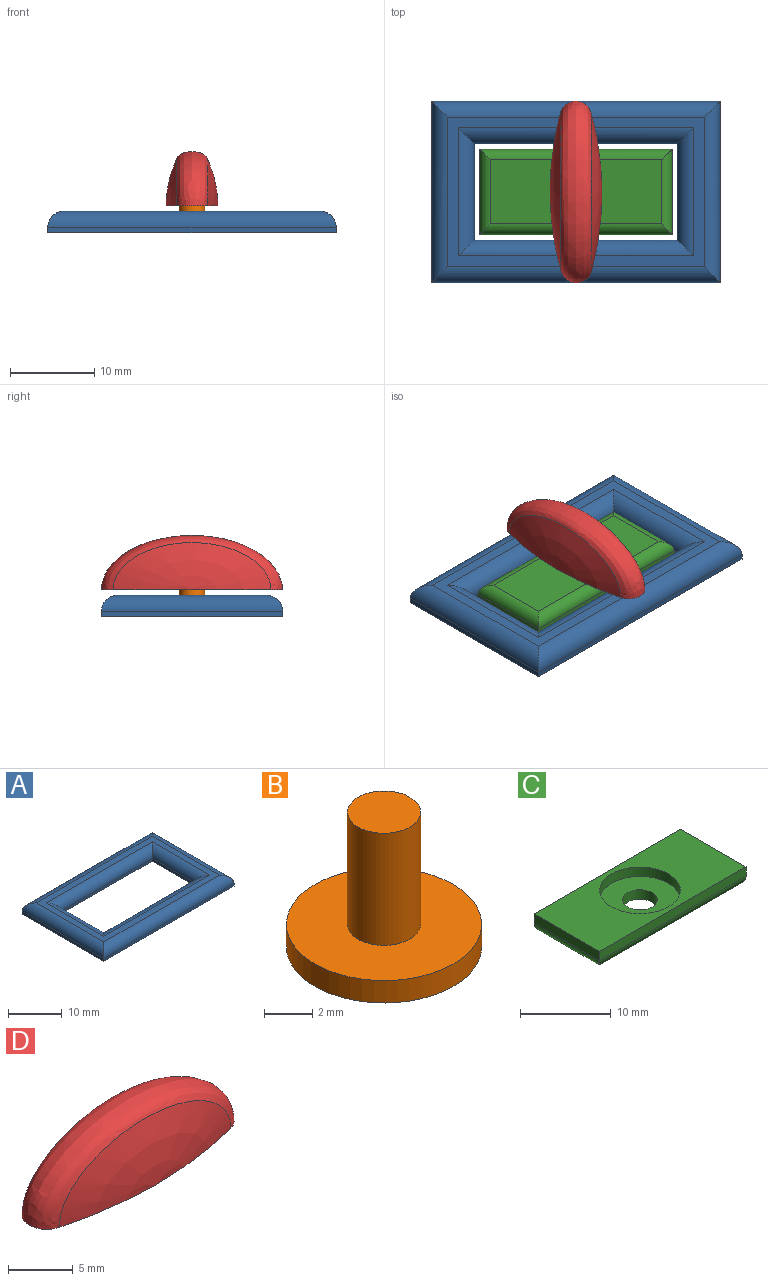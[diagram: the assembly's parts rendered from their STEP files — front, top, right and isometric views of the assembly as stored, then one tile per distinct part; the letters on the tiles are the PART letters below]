
ASSEMBLY  parts=4 mates=6
PART A: 18 faces, bbox 34.3x21.6x2.5 mm
  f0: plane 24.13x0.64mm, normal (0,1,0), area 15.3mm2, adj f1,f7,f9,f10
  f1: plane 11.43x0.64mm, normal (1,0,0), area 7.3mm2, adj f0,f2,f9,f11
  f2: plane 24.13x0.64mm, normal (0,-1,0), area 15.3mm2, adj f1,f7,f9,f13
  f3: plane 34.29x0.64mm, normal (0,-1,0), area 21.8mm2, adj f4,f6,f9,f15
  f4: plane 21.59x0.64mm, normal (1,0,0), area 13.7mm2, adj f3,f5,f9,f14
  f5: plane 34.29x0.64mm, normal (0,1,0), area 21.8mm2, adj f4,f6,f9,f16
  f6: plane 21.59x0.64mm, normal (-1,0,0), area 13.7mm2, adj f3,f5,f9,f17
  f7: plane 11.43x0.64mm, normal (-1,0,0), area 7.3mm2, adj f0,f2,f9,f12
  f8: plane 30.48x17.78mm, normal (0,0,1), area 116.1mm2, adj f10,f11,f12,f13,f14,f15,f16,f17
  f9: plane 34.29x21.59mm, normal (0,0,-1), area 464.5mm2, adj f0,f1,f2,f3,f4,f5,f6,f7
  f10: cylinder r=1.91mm len=27.94mm, axis (1,0,0), area 76.3mm2, adj f0,f8,f11,f12
  f11: cylinder r=1.91mm len=15.24mm, axis (0,-1,0), area 38.3mm2, adj f1,f8,f10,f13
  f12: cylinder r=1.91mm len=15.24mm, axis (0,1,0), area 38.3mm2, adj f7,f8,f10,f13
  f13: cylinder r=1.91mm len=27.94mm, axis (-1,0,0), area 76.3mm2, adj f2,f8,f11,f12
  f14: cylinder r=1.91mm len=21.59mm, axis (0,-1,0), area 60.5mm2, adj f4,f8,f15,f16
  f15: cylinder r=1.91mm len=34.29mm, axis (-1,0,0), area 98.5mm2, adj f3,f8,f14,f17
  f16: cylinder r=1.91mm len=34.29mm, axis (1,0,0), area 98.5mm2, adj f5,f8,f14,f17
  f17: cylinder r=1.91mm len=21.59mm, axis (0,1,0), area 60.5mm2, adj f6,f8,f15,f16
PART B: 5 faces, bbox 8.1x8.1x6.9 mm
  f0: cylinder r=4.06mm len=8.13mm, axis (0,0,-1), area 29.2mm2, adj f1,f2
  f1: plane 8.13x8.13mm, normal (0,0,1), area 44.6mm2, adj f0,f3
  f2: plane 8.13x8.13mm, normal (0,0,-1), area 51.9mm2, adj f0
  f3: cylinder r=1.52mm len=5.72mm, axis (0,0,-1), area 54.7mm2, adj f1,f4
  f4: plane 3.05x3.05mm, normal (0,0,1), area 7.3mm2, adj f3
PART C: 13 faces, bbox 22.9x10.2x2.5 mm
  f0: cylinder r=1.91mm len=3.81mm, axis (0,0,1), area 15.2mm2, adj f6,f12
  f1: plane 22.86x1.27mm, normal (0,-1,0), area 29mm2, adj f2,f4,f5,f7
  f2: plane 10.16x1.27mm, normal (1,0,0), area 12.9mm2, adj f1,f3,f5,f9
  f3: plane 22.86x1.27mm, normal (0,1,0), area 29mm2, adj f2,f4,f5,f10
  f4: plane 10.16x1.27mm, normal (-1,0,0), area 12.9mm2, adj f1,f3,f5,f8
  f5: plane 22.86x10.16mm, normal (0,0,1), area 170.2mm2, adj f1,f2,f3,f4,f11
  f6: plane 20.32x7.62mm, normal (0,0,-1), area 143.4mm2, adj f0,f7,f8,f9,f10
  f7: cylinder r=1.27mm len=22.86mm, axis (1,0,0), area 43.8mm2, adj f1,f6,f8,f9
  f8: cylinder r=1.27mm len=10.16mm, axis (0,-1,0), area 18.4mm2, adj f4,f6,f7,f10
  f9: cylinder r=1.27mm len=10.16mm, axis (0,1,0), area 18.4mm2, adj f2,f6,f7,f10
  f10: cylinder r=1.27mm len=22.86mm, axis (-1,0,0), area 43.8mm2, adj f3,f6,f8,f9
  f11: cylinder r=4.45mm len=8.89mm, axis (0,0,1), area 35.5mm2, adj f5,f12
  f12: plane 8.89x8.89mm, normal (0,0,1), area 50.7mm2, adj f0,f11
PART D: 6 faces, bbox 144.1x137.9x172.9 mm
  f0: bspline ~25.91x21.59mm, area 118.6mm2, adj f1,f2,f3
  f1: bspline ~172.89x144.07mm, area 85.8mm2, adj f0,f3
  f2: bspline ~172.89x144.07mm, area 85.8mm2, adj f0,f3
  f3: plane 21.59x6.17mm, normal (0,0,-1), area 98mm2, adj f0,f1,f2,f4
  f4: cylinder r=1.78mm len=3.81mm, axis (0,0,-1), area 42.6mm2, adj f3,f5
  f5: plane 3.56x3.56mm, normal (0,0,-1), area 9.9mm2, adj f4
PLACE A at identity
PLACE B t=(0,0,0.13)mm
PLACE C rot(axis=(1,0,0),180deg) t=(0,0,2.54)mm
PLACE D rot(axis=(0,0,-1),89.8deg) t=(0,0,3.17)mm
MATE planar B.f0 <-> C.f11  axis (0,0,1) through (0,0,1.27)mm
MATE slider B.f3 <-> C.f0  axis (0,0,-1) through (0,0,4.13)mm
MATE planar D.f4 <-> B.f3  axis (0,0,-1) through (0,0,6.99)mm
MATE slider C.f0 <-> A.f9  axis (0,0,1) through (0,0,2.54)mm
MATE cylindrical D.f4 <-> B.f3  axis (0,0,-1) through (0,0,3.17)mm
MATE planar C.f11 <-> A.f9  axis (0,0,-1) through (0,0,0)mm
